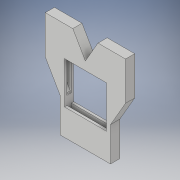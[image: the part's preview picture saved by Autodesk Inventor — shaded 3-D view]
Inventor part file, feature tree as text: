
AUTODESK INVENTOR PART (.ipt)
format: ipt  version: 2017 (Build 210142000, 142)  size: 259,584 bytes
history: native  units: in
note: dims shown in document units (in); Inventor stores cm internally (conversion verified against a paired STEP export)
features: extrude x6, sketch x6, other x3
ambient origin geometry x8: Origin, YZ Plane, XZ Plane, XY Plane, X Axis, Y Axis, Z Axis, Center Point
bodies: Body1 (feature_tree)
feature tree (15):
  other  "rame of door"
  extrude  "frame"  Depth=100.0in
  other  "middle of part"
  extrude  "door slot bottom"  Depth=10.0in
  extrude  "top left and right slots"  Depth=10.0in
  extrude  "door recieves"  Depth=22.0in
  extrude  "front hide door"  Depth=10.0in TaperAngle=0.0deg
  extrude  "gap for door pieces"  Depth=2.0in
  other  "mate for door pieces"
  sketch  "Sketch1"  dims[d0=100.0in d1=100.0in]
  sketch  "Sketch7"  dims[d3=10.0in d4=10.0in]
  sketch  "Sketch8"  dims[d5=10.0in d6=10.0in]
  sketch  "Sketch13"  dims[d7=22.0in d8=0.0in d118=0.7071in d178=0.8316in]
  sketch  "Sketch14"  dims[d459=10.0in d460=0.0in d865=10.0in d866=0.0in]
  sketch  "Sketch15"  dims[d878=60.0deg d889=2.0in d901=2.0in d903=51.0in d907=10.0in d916=10.0in d917=10.0in d919=10.0in d920=10.0in d921=10.0in d922=22.0in d923=0.0in d926=25.7957in d927=52.0in d928=21.0in d929=0.0in d930=10.0in d931=0.0in d932=50.0in]
